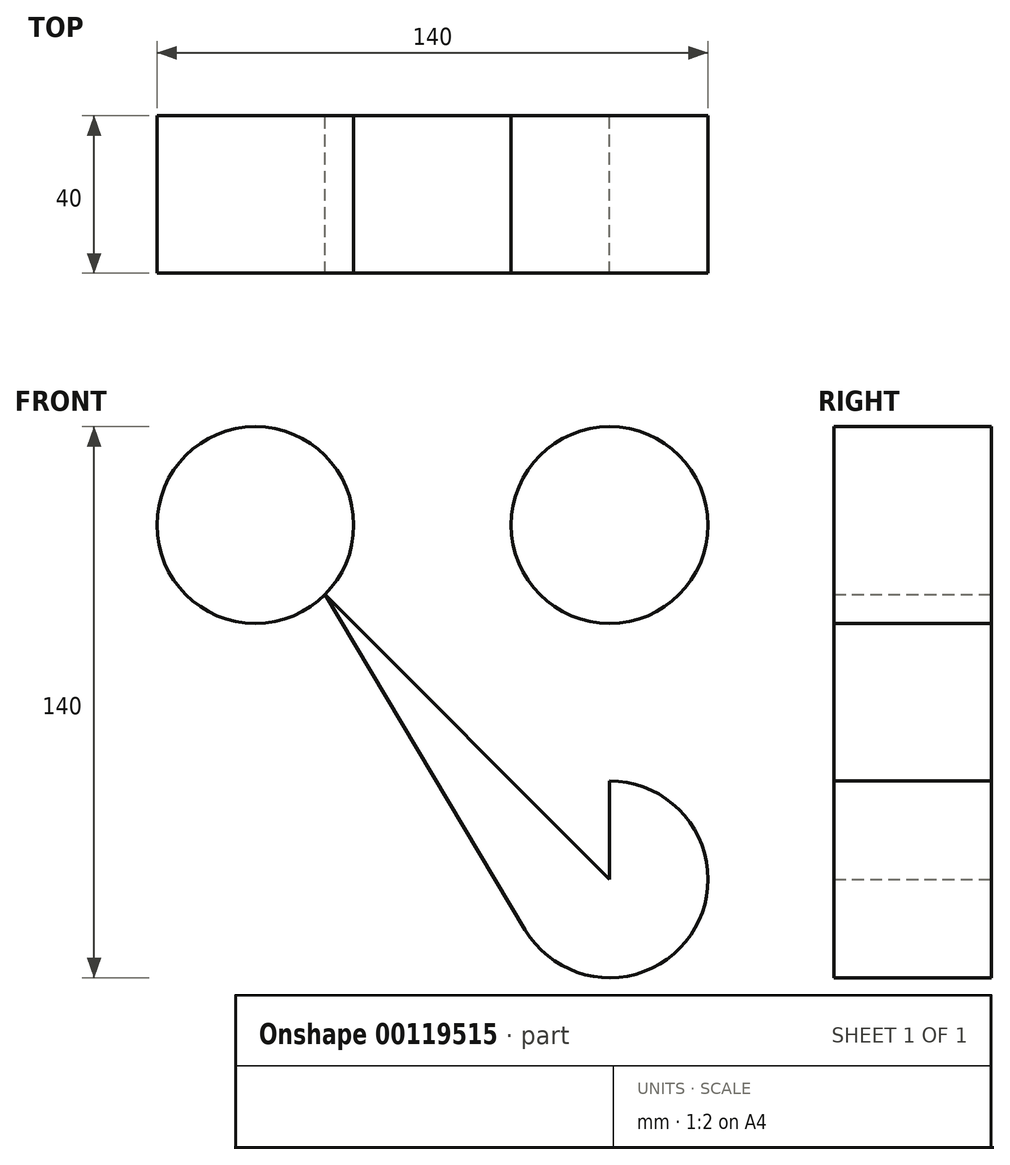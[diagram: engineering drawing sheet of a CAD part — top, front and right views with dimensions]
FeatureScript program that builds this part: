
annotation { "Feature Type Name" : "Feature", "Feature Type Description" : "" }
export const myFeature = defineFeature(function(context is Context, id is Id, definition is map)
    precondition{}
    {
        {
            var Q0;
            Q0=qCreatedBy(makeId("Front.planeOp"),FACE);
            var sketch = newSketch(context, id + "F0", { "sketchPlane" : qUnion([Q0])});
            skCircle(sketch, "E0", {"center": v(0, 0) * mm, "radius": 25 * mm});
            skCircle(sketch, "E1", {"center": v(0, 90) * mm, "radius": 25 * mm});
            skCircle(sketch, "E2", {"center": v(-90, 90) * mm, "radius": 25 * mm});
            skLineSegment(sketch, "E3", {"start": v(-90, 90) * mm, "end": v(0, 0) * mm});
            skLineSegment(sketch, "E4", {"start": v(-90, 90) * mm, "end": v(0, 90) * mm, "construction": true});
            skLineSegment(sketch, "E5", {"start": v(0, 90) * mm, "end": v(0, 0) * mm});
            skLineSegment(sketch, "E6", {"start": v(-72.32, 72.32) * mm, "end": v(-21.46, -12.82) * mm});
            skSolve(sketch);
        }
        {
            var Q0;
            {var subQ0=sQuery(id+"F0.wireOp",EDGE,"E0");var subQ1=makeQuery(id+"F0.imprint","INTERSECT",VERTEX,{"derivedFrom":[subQ0,sQuery(id+"F0.wireOp",EDGE,"E6")]});Q0=makeQuery(id+"F0.imprint","IMPRINT",FACE,{"disambiguationData":[TD([[makeQuery(id+"F0.imprint","IMPRINT",EDGE,{"disambiguationData":[TD([[subQ1,1.0]])],"derivedFrom":subQ0}),1.0]])]});}
            var Q1;
            {var subQ0=sQuery(id+"F0.wireOp",EDGE,"E6");Q1=makeQuery(id+"F0.imprint","IMPRINT",FACE,{"disambiguationData":[TD([[makeQuery(id+"F0.imprint","IMPRINT",EDGE,{"derivedFrom":subQ0}),1.0]])]});}
            var Q2;
            Q2=makeQuery(id+"F0.imprint","IMPRINT",FACE,{"disambiguationData":[TD([[makeQuery(id+"F0.imprint","IMPRINT",EDGE,{"derivedFrom":sQuery(id+"F0.wireOp",EDGE,"E2")}),1.0]])]});
            var Q3;
            Q3=makeQuery(id+"F0.imprint","IMPRINT",FACE,{"disambiguationData":[TD([[makeQuery(id+"F0.imprint","IMPRINT",EDGE,{"derivedFrom":sQuery(id+"F0.wireOp",EDGE,"E1")}),1.0]])]});
            extrude(context, id + "F1", {"entities" : qUnion([Q0, Q1, Q2, Q3]), "endBound" : BoundingType.SYMMETRIC, "depth" : 40 * mm});
        }
    });
